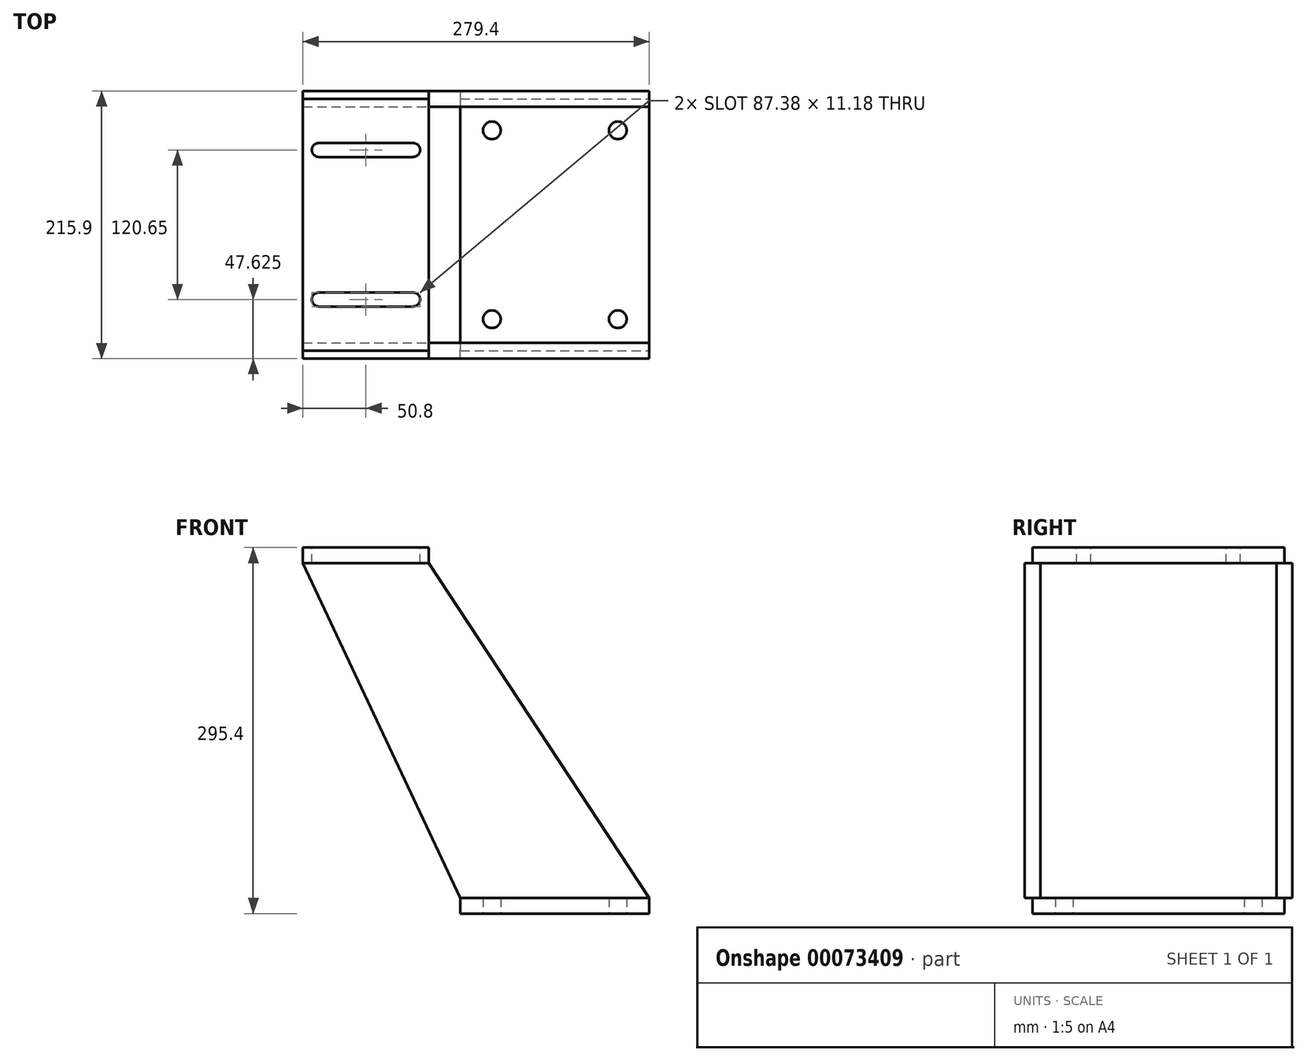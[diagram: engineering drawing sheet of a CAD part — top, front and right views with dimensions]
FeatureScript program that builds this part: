
annotation { "Feature Type Name" : "Feature", "Feature Type Description" : "" }
export const myFeature = defineFeature(function(context is Context, id is Id, definition is map)
    precondition{}
    {
        {
            var Q0;
            Q0=qCreatedBy(makeId("Top.planeOp"),FACE);
            var sketch = newSketch(context, id + "F0", { "sketchPlane" : qUnion([Q0])});
            skLineSegment(sketch, "E0.rect.bottom", {"start": v(-76.2, 101.6) * mm, "end": v(76.2, 101.6) * mm});
            skLineSegment(sketch, "E0.rect.top", {"start": v(-76.2, -101.6) * mm, "end": v(76.2, -101.6) * mm});
            skLineSegment(sketch, "E0.rect.left", {"start": v(-76.2, 101.6) * mm, "end": v(-76.2, -101.6) * mm});
            skLineSegment(sketch, "E0.rect.right", {"start": v(76.2, 101.6) * mm, "end": v(76.2, -101.6) * mm});
            skPoint(sketch, "E0.rect.middle", {"position": v(0, 0) * mm});
            skLineSegment(sketch, "E1.0", {"start": v(-50.8, 76.2) * mm, "end": v(50.8, 76.2) * mm, "construction": true});
            skLineSegment(sketch, "E1.1", {"start": v(-50.8, 76.2) * mm, "end": v(-50.8, -76.2) * mm, "construction": true});
            skLineSegment(sketch, "E1.2", {"start": v(-50.8, -76.2) * mm, "end": v(50.8, -76.2) * mm, "construction": true});
            skLineSegment(sketch, "E1.3", {"start": v(50.8, 76.2) * mm, "end": v(50.8, -76.2) * mm, "construction": true});
            skCircle(sketch, "E2", {"center": v(-50.8, 76.2) * mm, "radius": 7.14 * mm});
            skCircle(sketch, "E3", {"center": v(50.8, 76.2) * mm, "radius": 7.14 * mm});
            skCircle(sketch, "E4", {"center": v(-50.8, -76.2) * mm, "radius": 7.14 * mm});
            skCircle(sketch, "E5", {"center": v(50.8, -76.2) * mm, "radius": 7.14 * mm});
            skSolve(sketch);
        }
        {
            var Q0;
            Q0 = qSketchRegion(id + "F0", true);
            extrude(context, id + "F1", {"entities" : qUnion([Q0]), "depth" : 12.7 * mm});
        }
        {
            var Q0;
            Q0=makeQuery(id+"F1.opExtrude","CAP_FACE",FACE,{"disambiguationData":[OSD([sQuery(id+"F0.wireOp",EDGE,"E0.rect.bottom"),sQuery(id+"F0.wireOp",EDGE,"E0.rect.top"),sQuery(id+"F0.wireOp",EDGE,"E0.rect.left"),sQuery(id+"F0.wireOp",EDGE,"E0.rect.right"),sQuery(id+"F0.wireOp",EDGE,"E2"),sQuery(id+"F0.wireOp",EDGE,"E3"),sQuery(id+"F0.wireOp",EDGE,"E4"),sQuery(id+"F0.wireOp",EDGE,"E5")])],"isStart":true});
            cPlane(context, id + "F2", {"entities" : qUnion([Q0]), "cplaneType" : CPlaneType.OFFSET, "offset" : 295.4 * mm, "oppositeDirection" : true, "width" : 152.4 * mm, "height" : 152.4 * mm});
        }
        {
            var Q0;
            Q0=qCreatedBy(id+"F2.planeOp",FACE);
            var sketch = newSketch(context, id + "F3", { "sketchPlane" : qUnion([Q0])});
            skLineSegment(sketch, "E6", {"start": v(0, 185.97) * mm, "end": v(0, -193.47) * mm, "construction": true});
            skLineSegment(sketch, "E7.0", {"start": v(-152.4, 185.97) * mm, "end": v(-152.4, -193.47) * mm, "construction": true});
            skLineSegment(sketch, "E8", {"start": v(107.18, 0) * mm, "end": v(-288.33, 0) * mm, "construction": true});
            skLineSegment(sketch, "E9.rect.bottom", {"start": v(-203.2, 101.6) * mm, "end": v(-101.6, 101.6) * mm});
            skLineSegment(sketch, "E9.rect.top", {"start": v(-203.2, -101.6) * mm, "end": v(-101.6, -101.6) * mm});
            skLineSegment(sketch, "E9.rect.left", {"start": v(-203.2, 101.6) * mm, "end": v(-203.2, -101.6) * mm});
            skLineSegment(sketch, "E9.rect.right", {"start": v(-101.6, 101.6) * mm, "end": v(-101.6, -101.6) * mm});
            skPoint(sketch, "E9.rect.middle", {"position": v(-152.4, 0) * mm});
            skLineSegment(sketch, "E10.0", {"start": v(107.18, 60.33) * mm, "end": v(-288.33, 60.32) * mm, "construction": true});
            skLineSegment(sketch, "E11.0", {"start": v(-190.5, 185.97) * mm, "end": v(-190.5, -193.47) * mm, "construction": true});
            skLineSegment(sketch, "E12.0", {"start": v(-114.3, 185.97) * mm, "end": v(-114.3, -193.47) * mm, "construction": true});
            skLineSegment(sketch, "E13", {"start": v(-190.5, 60.32) * mm, "end": v(-114.3, 60.32) * mm});
            skArc(sketch, "E14.0.startCap", {"start": v(-190.5, 54.74) * mm, "mid": v(-196.09, 60.32) * mm, "end": v(-190.5, 65.91) * mm});
            skArc(sketch, "E14.0.endCap", {"start": v(-114.3, 65.91) * mm, "mid": v(-108.71, 60.32) * mm, "end": v(-114.3, 54.74) * mm});
            skLineSegment(sketch, "E14.0.left", {"start": v(-190.5, 65.91) * mm, "end": v(-114.3, 65.91) * mm});
            skLineSegment(sketch, "E14.0.right", {"start": v(-190.5, 54.74) * mm, "end": v(-114.3, 54.74) * mm});
            skArc(sketch, "E15.MirrorCS", {"start": v(-114.3, -65.91) * mm, "mid": v(-108.71, -60.32) * mm, "end": v(-114.3, -54.74) * mm});
            skArc(sketch, "E16.MirrorCS", {"start": v(-190.5, -54.74) * mm, "mid": v(-196.09, -60.32) * mm, "end": v(-190.5, -65.91) * mm});
            skLineSegment(sketch, "E17.MirrorCS", {"start": v(-190.5, -54.74) * mm, "end": v(-114.3, -54.74) * mm});
            skLineSegment(sketch, "E18.MirrorCS", {"start": v(-190.5, -65.91) * mm, "end": v(-114.3, -65.91) * mm});
            skLineSegment(sketch, "E19.MirrorCS", {"start": v(-190.5, -60.32) * mm, "end": v(-114.3, -60.32) * mm});
            skSolve(sketch);
        }
        {
            var Q0;
            Q0 = qSketchRegion(id + "F3", true);
            extrude(context, id + "F4", {"entities" : qUnion([Q0]), "depth" : 12.7 * mm});
        }
        {
            var Q0;
            Q0=makeQuery(id+"F4.opExtrude","SWEPT_FACE",FACE,{"disambiguationData":[OSD([sQuery(id+"F3.wireOp",EDGE,"E9.rect.top")])]});
            var sketch = newSketch(context, id + "F5", { "sketchPlane" : qUnion([Q0])});
            skLineSegment(sketch, "E20.0", {"start": v(76.2, 12.7) * mm, "end": v(-76.2, 12.7) * mm});
            skLineSegment(sketch, "E21.0", {"start": v(203.2, 282.7) * mm, "end": v(101.6, 282.7) * mm});
            skLineSegment(sketch, "E22", {"start": v(203.2, 282.7) * mm, "end": v(76.2, 12.7) * mm});
            skLineSegment(sketch, "E23", {"start": v(101.6, 282.7) * mm, "end": v(-76.2, 12.7) * mm});
            skSolve(sketch);
        }
        {
            var Q0;
            Q0 = qSketchRegion(id + "F5", true);
            extrude(context, id + "F6", {"entities" : qUnion([Q0]), "endBound" : BoundingType.SYMMETRIC, "depth" : 12.7 * mm});
        }
        {
            var Q0;
            Q0=makeQuery(id+"F6.opExtrude","SWEPT_BODY",BODY,{"disambiguationData":[OSD([sQuery(id+"F5.wireOp",EDGE,"f1f27c51-49fc-4245-874a-efe3231ee20e.0"),sQuery(id+"F5.wireOp",EDGE,"E20.0"),sQuery(id+"F5.wireOp",EDGE,"P7uxkj9T-qamm-GDIi-5Cy6-n8MuDFCQXTvc"),sQuery(id+"F5.wireOp",EDGE,"06WD7JD2-YMt4-Fifx-PtCd-SJVudk0IbHSt")])]});
            var Q1;
            Q1=qCreatedBy(makeId("Front.planeOp"),FACE);
            mirror(context, id + "F7", {"entities" : qUnion([Q0]), "mirrorPlane" : qUnion([Q1])});
        }
    });
